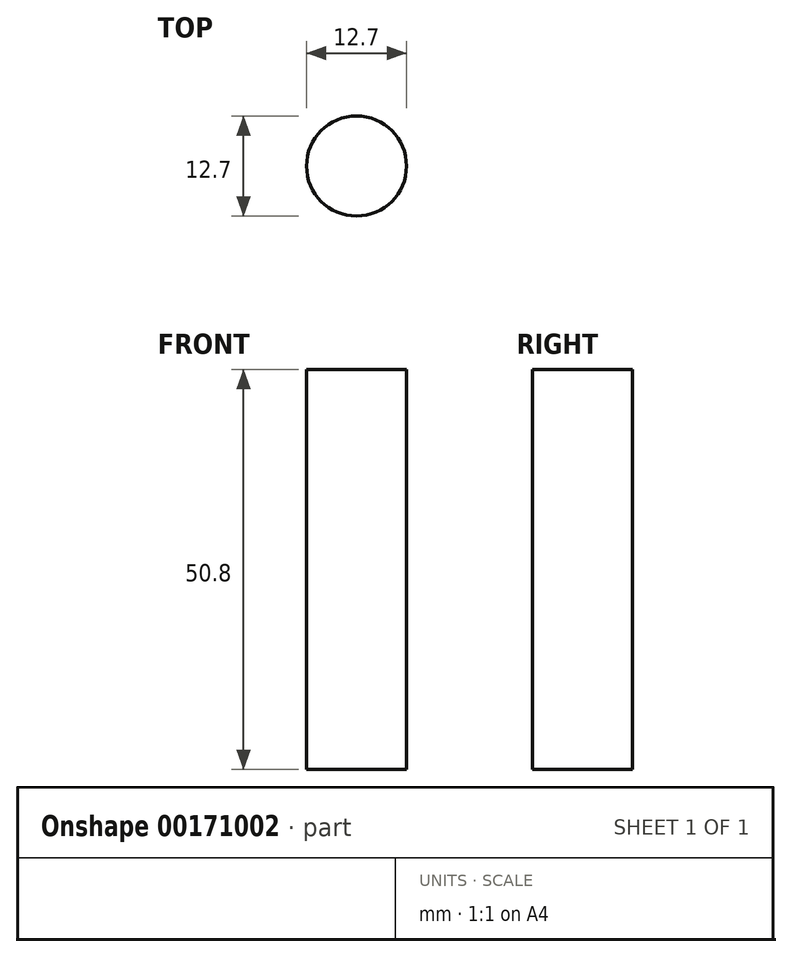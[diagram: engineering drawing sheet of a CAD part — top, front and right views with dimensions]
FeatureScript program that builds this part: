
annotation { "Feature Type Name" : "Feature", "Feature Type Description" : "" }
export const myFeature = defineFeature(function(context is Context, id is Id, definition is map)
    precondition{}
    {
        {
            var Q0;
            Q0=qCreatedBy(makeId("Top.planeOp"),FACE);
            var sketch = newSketch(context, id + "F0", { "sketchPlane" : qUnion([Q0])});
            skCircle(sketch, "E0", {"center": v(0, 0) * mm, "radius": 6.35 * mm});
            skSolve(sketch);
        }
        {
            var Q0;
            Q0=makeQuery(id+"F0.imprint","IMPRINT",FACE,{"disambiguationData":[TD([[makeQuery(id+"F0.imprint","IMPRINT",EDGE,{"derivedFrom":sQuery(id+"F0.wireOp",EDGE,"E0")}),1.0]])]});
            extrude(context, id + "F1", {"entities" : qUnion([Q0]), "depth" : 50.8 * mm});
        }
    });
